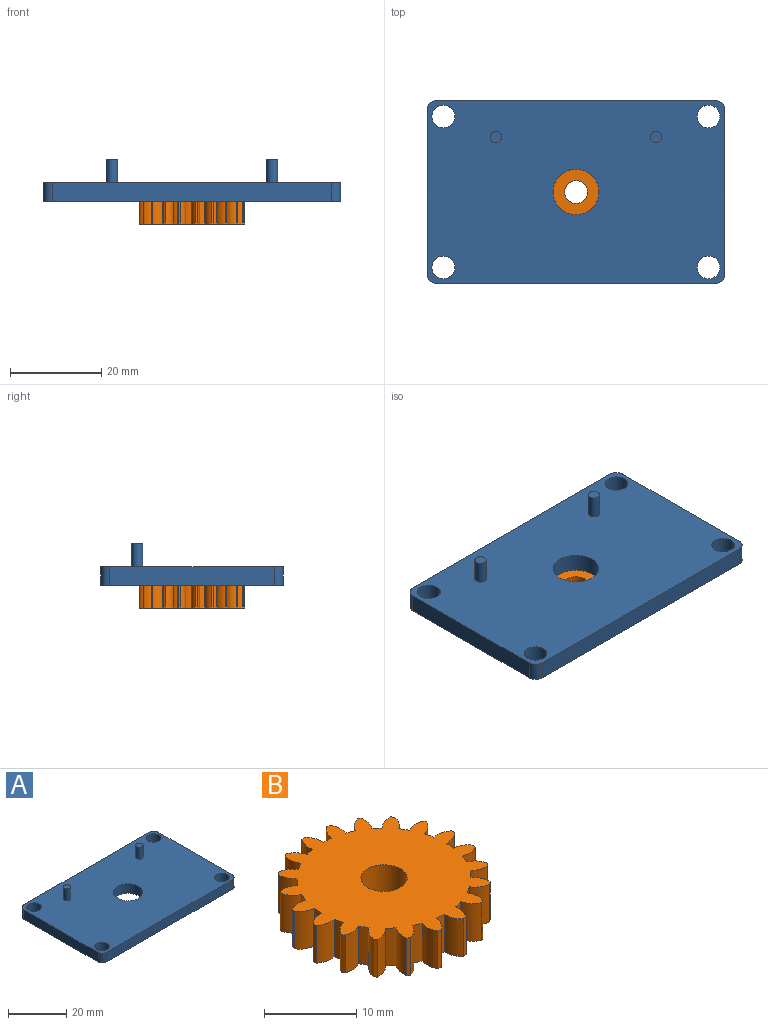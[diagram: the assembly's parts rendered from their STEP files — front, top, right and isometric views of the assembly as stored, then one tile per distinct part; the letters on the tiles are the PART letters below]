
ASSEMBLY  parts=2 mates=2
PART A: 19 faces, bbox 65x40x9 mm
  f0: plane 61x4mm, normal (0,1,0), area 244mm2, adj f4,f5,f11,f14
  f1: plane 36x4mm, normal (-1,0,0), area 144mm2, adj f4,f5,f11,f12
  f2: plane 61x4mm, normal (0,-1,0), area 244mm2, adj f4,f5,f12,f13
  f3: plane 36x4mm, normal (1,0,0), area 144mm2, adj f4,f5,f13,f14
  f4: plane 65x40mm, normal (0,0,1), area 2429.7mm2, adj f0,f1,f2,f3,f6,f7,f9,f11
  f5: plane 65x40mm, normal (0,0,-1), area 2439.5mm2, adj f0,f1,f2,f3,f6,f11,f12,f13
  f6: cylinder r=5mm len=10mm, axis (0,0,1), area 125.7mm2, adj f4,f5
  f7: cylinder r=1.25mm len=5mm, axis (0,0,-1), area 39.3mm2, adj f4,f8
  f8: plane 2.5x2.5mm, normal (0,0,1), area 4.9mm2, adj f7
  f9: cylinder r=1.25mm len=5mm, axis (0,0,-1), area 39.3mm2, adj f4,f10
  f10: plane 2.5x2.5mm, normal (0,0,1), area 4.9mm2, adj f9
  f11: cylinder r=2mm len=4mm, axis (0,0,-1), area 12.6mm2, adj f0,f1,f4,f5
  f12: cylinder r=2mm len=4mm, axis (0,0,1), area 12.6mm2, adj f1,f2,f4,f5
  f13: cylinder r=2mm len=4mm, axis (0,0,-1), area 12.6mm2, adj f2,f3,f4,f5
  f14: cylinder r=2mm len=4mm, axis (0,0,1), area 12.6mm2, adj f0,f3,f4,f5
  f15: cylinder r=2.5mm len=5mm, axis (0,0,1), area 62.8mm2, adj f4,f5
  f16: cylinder r=2.5mm len=5mm, axis (0,0,1), area 62.8mm2, adj f4,f5
  f17: cylinder r=2.5mm len=5mm, axis (0,0,1), area 62.8mm2, adj f4,f5
  f18: cylinder r=2.5mm len=5mm, axis (0,0,1), area 62.8mm2, adj f4,f5
PART B: 83 faces, bbox 23x23x5 mm
  f0: cylinder r=2.61mm len=5mm, axis (0,0,-1), area 11.5mm2, adj f1,f79,f81,f82
  f1: cylinder r=9.41mm len=5mm, axis (0,0,-1), area 5.9mm2, adj f0,f2,f81,f82
  f2: cylinder r=2.61mm len=5mm, axis (0,0,-1), area 11.5mm2, adj f1,f3,f81,f82
  f3: plane 5x0.41mm, normal (-0.38,0.92,0), area 2.2mm2, adj f2,f4,f81,f82
  f4: cylinder r=2.61mm len=5mm, axis (0,0,-1), area 11.5mm2, adj f3,f5,f81,f82
  f5: cylinder r=9.41mm len=5mm, axis (0,0,-1), area 5.9mm2, adj f4,f6,f81,f82
  f6: cylinder r=2.61mm len=5mm, axis (0,0,-1), area 11.5mm2, adj f5,f7,f81,f82
  f7: plane 5x0.34mm, normal (-0.65,0.76,0), area 2.2mm2, adj f6,f8,f81,f82
  f8: cylinder r=2.61mm len=5mm, axis (0,0,-1), area 11.5mm2, adj f7,f9,f81,f82
  f9: cylinder r=9.41mm len=5mm, axis (0,0,-1), area 5.9mm2, adj f8,f10,f81,f82
  f10: cylinder r=2.61mm len=5mm, axis (0,0,-1), area 11.5mm2, adj f9,f11,f81,f82
  f11: plane 5x0.38mm, normal (-0.85,0.52,0), area 2.2mm2, adj f10,f12,f81,f82
  f12: cylinder r=2.61mm len=5mm, axis (0,0,-1), area 11.5mm2, adj f11,f13,f81,f82
  f13: cylinder r=9.41mm len=5mm, axis (0,0,-1), area 5.9mm2, adj f12,f14,f81,f82
  f14: cylinder r=2.61mm len=5mm, axis (0,0,-1), area 11.5mm2, adj f13,f15,f81,f82
  f15: plane 5x0.43mm, normal (-0.97,0.23,0), area 2.2mm2, adj f14,f16,f81,f82
  f16: cylinder r=2.61mm len=5mm, axis (0,0,-1), area 11.5mm2, adj f15,f17,f81,f82
  f17: cylinder r=9.41mm len=5mm, axis (0,0,-1), area 5.9mm2, adj f16,f18,f81,f82
  f18: cylinder r=2.61mm len=5mm, axis (0,0,-1), area 11.5mm2, adj f17,f19,f81,f82
  f19: plane 5x0.44mm, normal (-1,-0.08,0), area 2.2mm2, adj f18,f20,f81,f82
  f20: cylinder r=2.61mm len=5mm, axis (0,0,-1), area 11.5mm2, adj f19,f21,f81,f82
  f21: cylinder r=9.41mm len=5mm, axis (0,0,-1), area 5.9mm2, adj f20,f22,f81,f82
  f22: cylinder r=2.61mm len=5mm, axis (0,0,-1), area 11.5mm2, adj f21,f23,f81,f82
  f23: plane 5x0.41mm, normal (-0.92,-0.38,0), area 2.2mm2, adj f22,f24,f81,f82
  f24: cylinder r=2.61mm len=5mm, axis (0,0,-1), area 11.5mm2, adj f23,f25,f81,f82
  f25: cylinder r=9.41mm len=5mm, axis (0,0,-1), area 5.9mm2, adj f24,f26,f81,f82
  f26: cylinder r=2.61mm len=5mm, axis (0,0,-1), area 11.5mm2, adj f25,f27,f81,f82
  f27: plane 5x0.34mm, normal (-0.76,-0.65,0), area 2.2mm2, adj f26,f28,f81,f82
  f28: cylinder r=2.61mm len=5mm, axis (0,0,-1), area 11.5mm2, adj f27,f29,f81,f82
  f29: cylinder r=9.41mm len=5mm, axis (0,0,-1), area 5.9mm2, adj f28,f30,f81,f82
  f30: cylinder r=2.61mm len=5mm, axis (0,0,-1), area 11.5mm2, adj f29,f31,f81,f82
  f31: plane 5x0.38mm, normal (-0.52,-0.85,0), area 2.2mm2, adj f30,f32,f81,f82
  f32: cylinder r=2.61mm len=5mm, axis (0,0,-1), area 11.5mm2, adj f31,f33,f81,f82
  f33: cylinder r=9.41mm len=5mm, axis (0,0,-1), area 5.9mm2, adj f32,f34,f81,f82
  f34: cylinder r=2.61mm len=5mm, axis (0,0,-1), area 11.5mm2, adj f33,f35,f81,f82
  f35: plane 5x0.43mm, normal (-0.23,-0.97,0), area 2.2mm2, adj f34,f36,f81,f82
  f36: cylinder r=2.61mm len=5mm, axis (0,0,-1), area 11.5mm2, adj f35,f37,f81,f82
  f37: cylinder r=9.41mm len=5mm, axis (0,0,-1), area 5.9mm2, adj f36,f38,f81,f82
  f38: cylinder r=2.61mm len=5mm, axis (0,0,-1), area 11.5mm2, adj f37,f39,f81,f82
  f39: plane 5x0.44mm, normal (0.08,-1,0), area 2.2mm2, adj f38,f40,f81,f82
  f40: cylinder r=2.61mm len=5mm, axis (0,0,-1), area 11.5mm2, adj f39,f41,f81,f82
  f41: cylinder r=9.41mm len=5mm, axis (0,0,-1), area 5.9mm2, adj f40,f42,f81,f82
  f42: cylinder r=2.61mm len=5mm, axis (0,0,-1), area 11.5mm2, adj f41,f43,f81,f82
  f43: plane 5x0.41mm, normal (0.38,-0.92,0), area 2.2mm2, adj f42,f44,f81,f82
  f44: cylinder r=2.61mm len=5mm, axis (0,0,-1), area 11.5mm2, adj f43,f45,f81,f82
  f45: cylinder r=9.41mm len=5mm, axis (0,0,-1), area 5.9mm2, adj f44,f46,f81,f82
  f46: cylinder r=2.61mm len=5mm, axis (0,0,-1), area 11.5mm2, adj f45,f47,f81,f82
  f47: plane 5x0.34mm, normal (0.65,-0.76,0), area 2.2mm2, adj f46,f48,f81,f82
  f48: cylinder r=2.61mm len=5mm, axis (0,0,-1), area 11.5mm2, adj f47,f49,f81,f82
  f49: cylinder r=9.41mm len=5mm, axis (0,0,-1), area 5.9mm2, adj f48,f50,f81,f82
  f50: cylinder r=2.61mm len=5mm, axis (0,0,-1), area 11.5mm2, adj f49,f51,f81,f82
  f51: plane 5x0.38mm, normal (0.85,-0.52,0), area 2.2mm2, adj f50,f52,f81,f82
  f52: cylinder r=2.61mm len=5mm, axis (0,0,-1), area 11.5mm2, adj f51,f53,f81,f82
  f53: cylinder r=9.41mm len=5mm, axis (0,0,-1), area 5.9mm2, adj f52,f54,f81,f82
  f54: cylinder r=2.61mm len=5mm, axis (0,0,-1), area 11.5mm2, adj f53,f55,f81,f82
  f55: plane 5x0.43mm, normal (0.97,-0.23,0), area 2.2mm2, adj f54,f56,f81,f82
  f56: cylinder r=2.61mm len=5mm, axis (0,0,-1), area 11.5mm2, adj f55,f57,f81,f82
  f57: cylinder r=9.41mm len=5mm, axis (0,0,-1), area 5.9mm2, adj f56,f58,f81,f82
  f58: cylinder r=2.61mm len=5mm, axis (0,0,-1), area 11.5mm2, adj f57,f59,f81,f82
  f59: plane 5x0.44mm, normal (1,0.08,0), area 2.2mm2, adj f58,f60,f81,f82
  f60: cylinder r=2.61mm len=5mm, axis (0,0,-1), area 11.5mm2, adj f59,f61,f81,f82
  f61: cylinder r=9.41mm len=5mm, axis (0,0,-1), area 5.9mm2, adj f60,f62,f81,f82
  f62: cylinder r=2.61mm len=5mm, axis (0,0,-1), area 11.5mm2, adj f61,f63,f81,f82
  f63: plane 5x0.41mm, normal (0.92,0.38,0), area 2.2mm2, adj f62,f64,f81,f82
  f64: cylinder r=2.61mm len=5mm, axis (0,0,-1), area 11.5mm2, adj f63,f65,f81,f82
  f65: cylinder r=9.41mm len=5mm, axis (0,0,-1), area 5.9mm2, adj f64,f66,f81,f82
  f66: cylinder r=2.61mm len=5mm, axis (0,0,-1), area 11.5mm2, adj f65,f67,f81,f82
  f67: plane 5x0.34mm, normal (0.76,0.65,0), area 2.2mm2, adj f66,f68,f81,f82
  f68: cylinder r=2.61mm len=5mm, axis (0,0,-1), area 11.5mm2, adj f67,f69,f81,f82
  f69: cylinder r=9.41mm len=5mm, axis (0,0,-1), area 5.9mm2, adj f68,f70,f81,f82
  f70: cylinder r=2.61mm len=5mm, axis (0,0,-1), area 11.5mm2, adj f69,f71,f81,f82
  f71: plane 5x0.38mm, normal (0.52,0.85,0), area 2.2mm2, adj f70,f72,f81,f82
  f72: cylinder r=2.61mm len=5mm, axis (0,0,-1), area 11.5mm2, adj f71,f73,f81,f82
  f73: cylinder r=9.41mm len=5mm, axis (0,0,-1), area 5.9mm2, adj f72,f74,f81,f82
  f74: cylinder r=2.61mm len=5mm, axis (0,0,-1), area 11.5mm2, adj f73,f75,f81,f82
  f75: plane 5x0.43mm, normal (0.23,0.97,0), area 2.2mm2, adj f74,f76,f81,f82
  f76: cylinder r=2.61mm len=5mm, axis (0,0,-1), area 11.5mm2, adj f75,f77,f81,f82
  f77: cylinder r=9.41mm len=5mm, axis (0,0,-1), area 5.9mm2, adj f76,f78,f81,f82
  f78: cylinder r=2.61mm len=5mm, axis (0,0,-1), area 11.5mm2, adj f77,f79,f81,f82
  f79: plane 5x0.44mm, normal (-0.08,1,0), area 2.2mm2, adj f0,f78,f81,f82
  f80: cylinder r=2.5mm len=5mm, axis (0,0,-1), area 78.5mm2, adj f81,f82
  f81: plane 22.96x22.96mm, normal (0,0,1), area 320mm2, adj f0,f1,f2,f3,f4,f5,f6,f7
  f82: plane 22.96x22.96mm, normal (0,0,-1), area 320mm2, adj f0,f1,f2,f3,f4,f5,f6,f7
PLACE A t=(-37.91,-3.33,-5.51)mm
PLACE B t=(-5.28,16.89,-10.51)mm
MATE planar B.f1 <-> A.f6  axis (0,0,1) through (-5.28,16.89,-5.51)mm
MATE cylindrical B.f1 <-> A.f6  axis (0,0,1) through (-5.28,16.89,-5.51)mm
